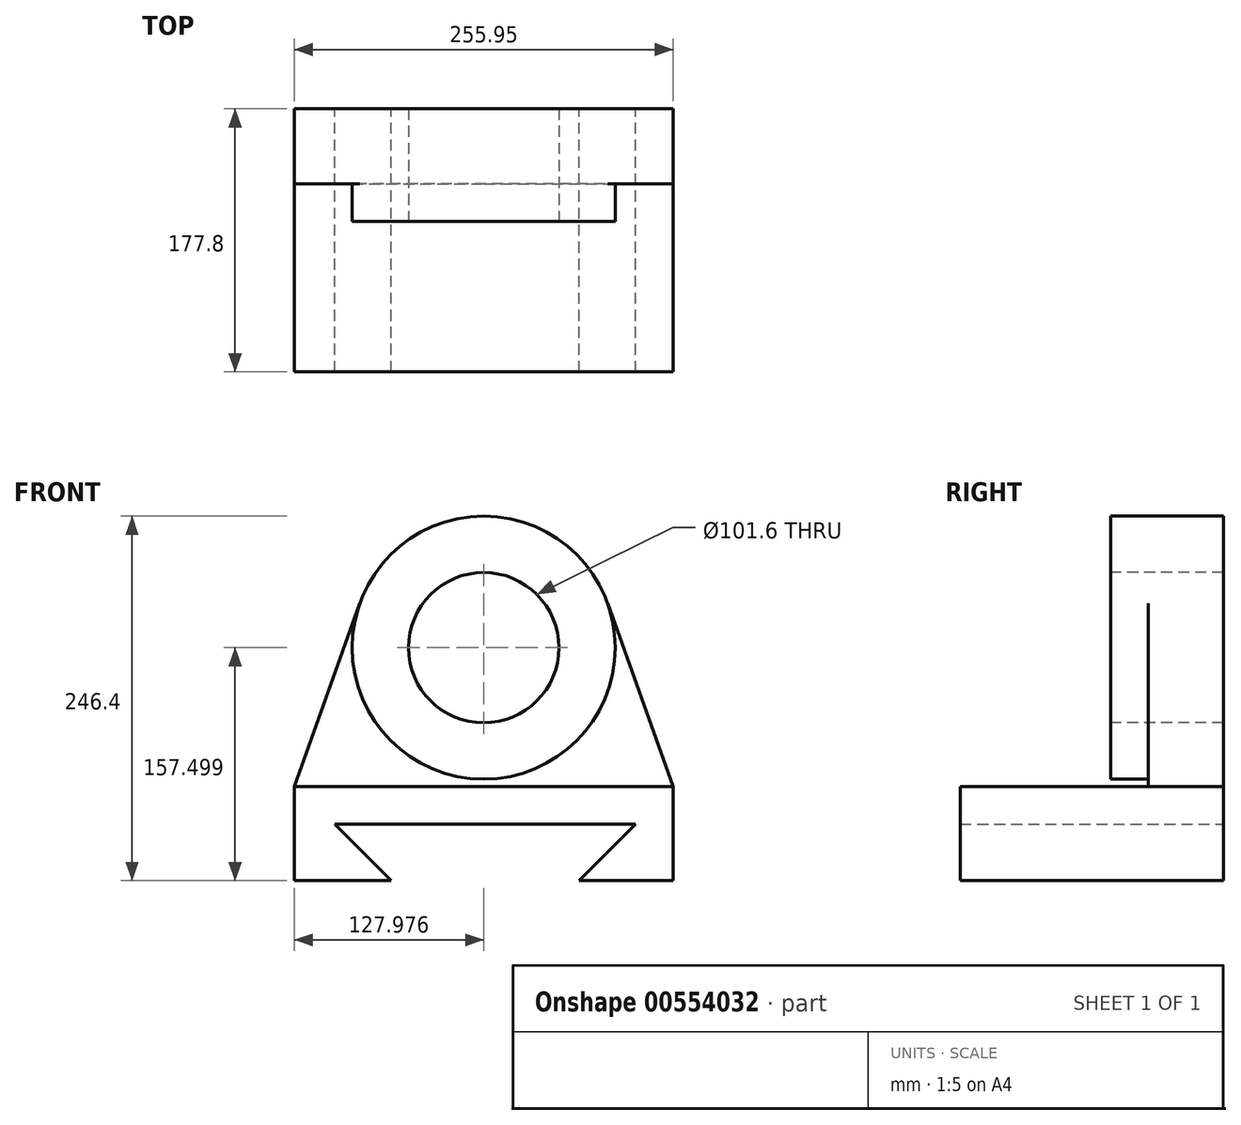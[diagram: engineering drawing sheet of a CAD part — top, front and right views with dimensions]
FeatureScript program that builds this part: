
annotation { "Feature Type Name" : "Feature", "Feature Type Description" : "" }
export const myFeature = defineFeature(function(context is Context, id is Id, definition is map)
    precondition{}
    {
        {
            var Q0;
            Q0=qCreatedBy(makeId("Front.planeOp"),FACE);
            var sketch = newSketch(context, id + "F0", { "sketchPlane" : qUnion([Q0])});
            skLineSegment(sketch, "E0", {"start": v(255.95, 121.36) * mm, "end": v(0, 121.36) * mm});
            skCircle(sketch, "E1", {"center": v(127.98, 215.36) * mm, "radius": 50.8 * mm});
            skPoint(sketch, "E1.centerSnap0", {"position": v(127.98, 121.36) * mm});
            skCircle(sketch, "E2", {"center": v(127.98, 215.36) * mm, "radius": 88.9 * mm});
            skLineSegment(sketch, "E3", {"start": v(255.95, 121.36) * mm, "end": v(211.7, 245.26) * mm});
            skLineSegment(sketch, "E4", {"start": v(0, 121.36) * mm, "end": v(44.26, 245.26) * mm});
            skLineSegment(sketch, "E5", {"start": v(0, 121.36) * mm, "end": v(0, 57.86) * mm});
            skLineSegment(sketch, "E6", {"start": v(255.95, 121.36) * mm, "end": v(255.95, 57.86) * mm});
            skLineSegment(sketch, "E7", {"start": v(255.95, 57.86) * mm, "end": v(192.45, 57.86) * mm});
            skLineSegment(sketch, "E8", {"start": v(192.45, 57.86) * mm, "end": v(230.55, 95.96) * mm});
            skLineSegment(sketch, "E9", {"start": v(230.55, 95.96) * mm, "end": v(27.35, 95.96) * mm});
            skLineSegment(sketch, "E10", {"start": v(27.35, 95.96) * mm, "end": v(65.45, 57.86) * mm});
            skLineSegment(sketch, "E11", {"start": v(65.45, 57.86) * mm, "end": v(0, 57.86) * mm});
            skSolve(sketch);
        }
        {
            var Q0;
            Q0=makeQuery(id+"F0.imprint","IMPRINT",FACE,{"disambiguationData":[TD([[makeQuery(id+"F0.imprint","IMPRINT",EDGE,{"derivedFrom":sQuery(id+"F0.wireOp",EDGE,"E0")}),1.0]])]});
            extrude(context, id + "F1", {"entities" : qUnion([Q0]), "depth" : 127 * mm, "offsetDistance" : 25.4 * mm});
        }
        {
            var Q0;
            Q0=makeQuery(id+"F0.imprint","IMPRINT",FACE,{"disambiguationData":[TD([[makeQuery(id+"F0.imprint","IMPRINT",EDGE,{"derivedFrom":sQuery(id+"F0.wireOp",EDGE,"E0")}),1.0]])]});
            var Q1;
            Q1=makeQuery(id+"F0.imprint","IMPRINT",FACE,{"disambiguationData":[TD([[makeQuery(id+"F0.imprint","IMPRINT",EDGE,{"derivedFrom":sQuery(id+"F0.wireOp",EDGE,"E1")}),-1.0]])]});
            var Q2;
            Q2=makeQuery(id+"F0.imprint","IMPRINT",FACE,{"disambiguationData":[TD([[makeQuery(id+"F0.imprint","IMPRINT",EDGE,{"derivedFrom":sQuery(id+"F0.wireOp",EDGE,"E0")}),-1.0]])]});
            extrude(context, id + "F2", {"entities" : qUnion([Q0, Q1, Q2]), "operationType" : NewBodyOperationType.ADD, "oppositeDirection" : true, "depth" : 50.8 * mm, "offsetDistance" : 25.4 * mm});
        }
        {
            var Q0;
            Q0=makeQuery(id+"F0.imprint","IMPRINT",FACE,{"disambiguationData":[TD([[makeQuery(id+"F0.imprint","IMPRINT",EDGE,{"derivedFrom":sQuery(id+"F0.wireOp",EDGE,"E1")}),-1.0]])]});
            extrude(context, id + "F3", {"entities" : qUnion([Q0]), "operationType" : NewBodyOperationType.ADD, "depth" : 25.4 * mm, "offsetDistance" : 25.4 * mm});
        }
    });
